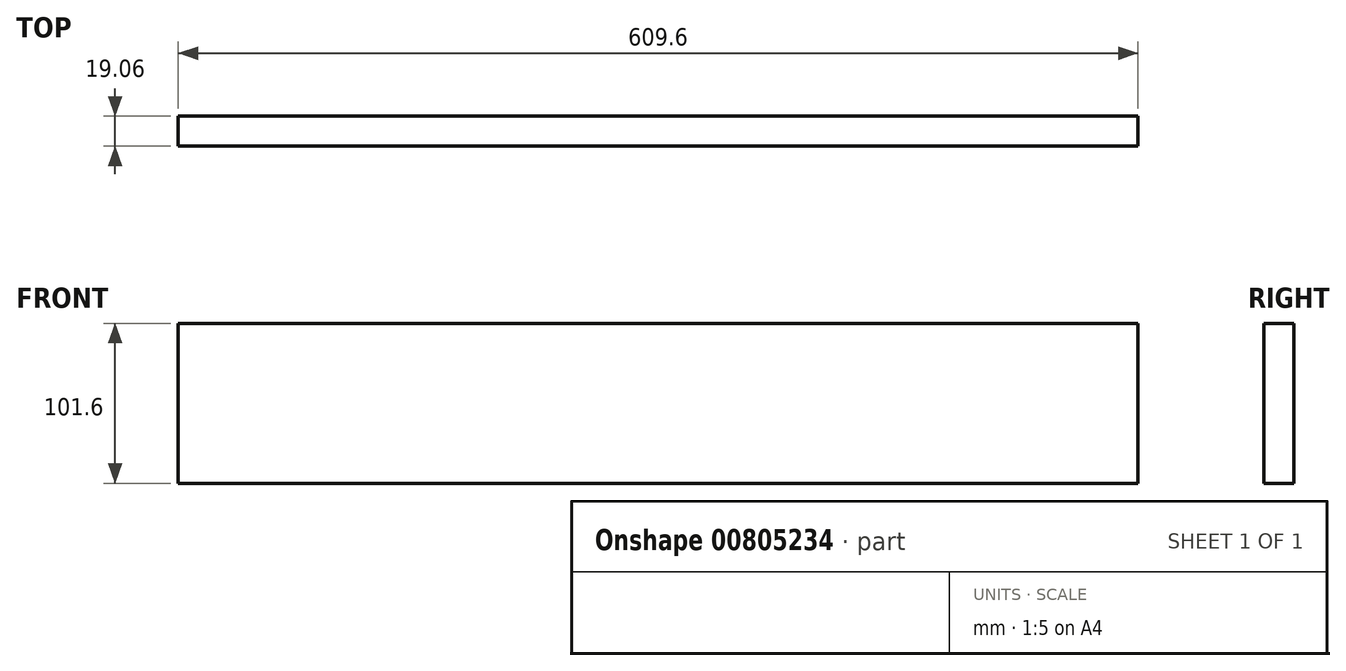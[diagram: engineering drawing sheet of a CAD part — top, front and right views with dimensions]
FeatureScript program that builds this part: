
annotation { "Feature Type Name" : "Feature", "Feature Type Description" : "" }
export const myFeature = defineFeature(function(context is Context, id is Id, definition is map)
    precondition{}
    {
        {
            var Q0;
            Q0=qCreatedBy(makeId("Front.planeOp"),FACE);
            var sketch = newSketch(context, id + "F0", { "sketchPlane" : qUnion([Q0])});
            skLineSegment(sketch, "E0.bottom", {"start": v(304.8, 50.8) * mm, "end": v(-304.8, 50.8) * mm});
            skLineSegment(sketch, "E0.top", {"start": v(304.8, -50.8) * mm, "end": v(-304.8, -50.8) * mm});
            skLineSegment(sketch, "E0.left", {"start": v(304.8, 50.8) * mm, "end": v(304.8, -50.8) * mm});
            skLineSegment(sketch, "E0.right", {"start": v(-304.8, 50.8) * mm, "end": v(-304.8, -50.8) * mm});
            skPoint(sketch, "E0.middle", {"position": v(0, 0) * mm});
            skSolve(sketch);
        }
        {
            var Q0;
            Q0=qSketchRegion(id+"F0",true);
            extrude(context, id + "F1", {"entities" : qUnion([Q0]), "endBound" : BoundingType.SYMMETRIC, "depth" : 19.05 * mm, "offsetDistance" : 25.4 * mm});
        }
    });
